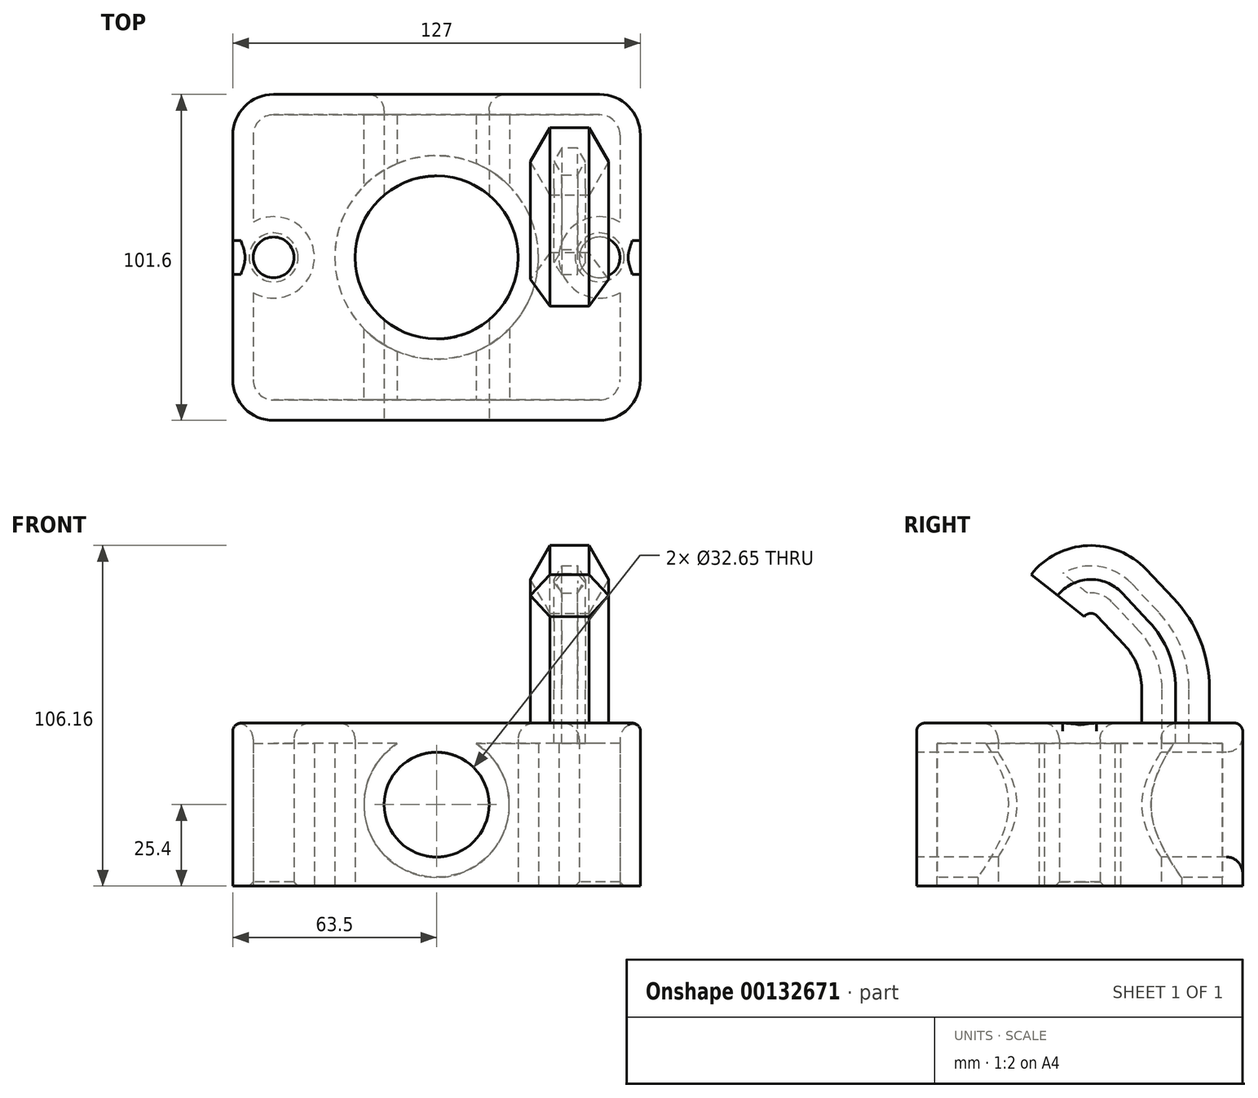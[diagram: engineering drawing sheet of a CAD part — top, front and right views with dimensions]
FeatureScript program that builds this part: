
annotation { "Feature Type Name" : "Feature", "Feature Type Description" : "" }
export const myFeature = defineFeature(function(context is Context, id is Id, definition is map)
    precondition{}
    {
        {
            var Q0;
            Q0=qCreatedBy(makeId("Top.planeOp"),FACE);
            var sketch = newSketch(context, id + "F0", { "sketchPlane" : qUnion([Q0])});
            skLineSegment(sketch, "E0.bottom", {"start": v(-63.5, 50.8) * mm, "end": v(63.5, 50.8) * mm});
            skLineSegment(sketch, "E0.top", {"start": v(-63.5, -50.8) * mm, "end": v(63.5, -50.8) * mm});
            skLineSegment(sketch, "E0.left", {"start": v(-63.5, 50.8) * mm, "end": v(-63.5, -50.8) * mm});
            skLineSegment(sketch, "E0.right", {"start": v(63.5, 50.8) * mm, "end": v(63.5, -50.8) * mm});
            skLineSegment(sketch, "E1", {"start": v(63.5, 50.8) * mm, "end": v(-63.5, -50.8) * mm, "construction": true});
            skCircle(sketch, "E2", {"center": v(0, 0) * mm, "radius": 25.4 * mm});
            skCircle(sketch, "E3", {"center": v(-50.8, 0) * mm, "radius": 6.35 * mm});
            skLineSegment(sketch, "E4", {"start": v(0, 0) * mm, "end": v(0, 50.8) * mm, "construction": true});
            skCircle(sketch, "E5.MirrorC", {"center": v(50.8, 0) * mm, "radius": 6.35 * mm});
            skSolve(sketch);
        }
        {
            var Q0;
            Q0 = qSketchRegion(id + "F0", true);
            extrude(context, id + "F1", {"entities" : qUnion([Q0]), "depth" : 50.8 * mm});
        }
        {
            var Q0;
            Q0=makeQuery(id+"F1.opExtrude","SWEPT_FACE",FACE,{"disambiguationData":[OSD([sQuery(id+"F0.wireOp",EDGE,"E0.top")])]});
            var sketch = newSketch(context, id + "F2", { "sketchPlane" : qUnion([Q0])});
            skCircle(sketch, "E6", {"center": v(0, 25.4) * mm, "radius": 16.33 * mm});
            skLineSegment(sketch, "E7", {"start": v(0, 0) * mm, "end": v(0, 50.8) * mm, "construction": true});
            skSolve(sketch);
        }
        {
            var Q0;
            Q0 = qSketchRegion(id + "F2", true);
            extrude(context, id + "F3", {"entities" : qUnion([Q0]), "operationType" : NewBodyOperationType.REMOVE, "endBound" : BoundingType.THROUGH_ALL, "oppositeDirection" : true, "depth" : 25.4 * mm});
        }
        {
            var Q0;
            Q0=makeQuery(id+"F1.opExtrude","CAP_EDGE",EDGE,{"disambiguationData":[OSD([sQuery(id+"F0.wireOp",EDGE,"E2")])],"isStart":false});
            var Q1;
            Q1=makeQuery(id+"F1.opExtrude","CAP_EDGE",EDGE,{"disambiguationData":[OSD([sQuery(id+"F0.wireOp",EDGE,"E3")])],"isStart":false});
            var Q2;
            Q2=makeQuery(id+"F1.opExtrude","CAP_EDGE",EDGE,{"disambiguationData":[OSD([sQuery(id+"F0.wireOp",EDGE,"E5.MirrorC")])],"isStart":false});
            var Q3;
            Q3=makeQuery(id+"F3.boolean.opBoolean","COPY",EDGE,{"derivedFrom":makeQuery(id+"F3.opExtrude","CAP_EDGE",EDGE,{"disambiguationData":[OSD([sQuery(id+"F2.wireOp",EDGE,"E6")])],"isStart":true})});
            var Q4;
            Q4=makeQuery(id+"F3.boolean.opBoolean","INTERSECT",EDGE,{"derivedFrom":[makeQuery(id+"F1.opExtrude","SWEPT_FACE",FACE,{"disambiguationData":[OSD([sQuery(id+"F0.wireOp",EDGE,"E0.bottom")])]}),makeQuery(id+"F3.opExtrude","SWEPT_FACE",FACE,{"disambiguationData":[OSD([sQuery(id+"F2.wireOp",EDGE,"E6")])]})]});
            fillet(context, id + "F4", {"entities" : qUnion([Q0, Q1, Q2, Q3, Q4]), "radius" : 5.08 * mm, "tangentPropagation" : true, "allowEdgeOverflow" : false});
        }
        {
            var Q0;
            Q0=makeQuery(id+"F1.opExtrude","SWEPT_EDGE",EDGE,{"disambiguationData":[OSD([sQuery(id+"F0.wireOp",EDGE,"E0.top"),sQuery(id+"F0.wireOp",EDGE,"E0.left")])]});
            var Q1;
            Q1=makeQuery(id+"F1.opExtrude","SWEPT_EDGE",EDGE,{"disambiguationData":[OSD([sQuery(id+"F0.wireOp",EDGE,"E0.top"),sQuery(id+"F0.wireOp",EDGE,"E0.right")])]});
            var Q2;
            Q2=makeQuery(id+"F1.opExtrude","SWEPT_EDGE",EDGE,{"disambiguationData":[OSD([sQuery(id+"F0.wireOp",EDGE,"E0.bottom"),sQuery(id+"F0.wireOp",EDGE,"E0.right")])]});
            var Q3;
            Q3=makeQuery(id+"F1.opExtrude","SWEPT_EDGE",EDGE,{"disambiguationData":[OSD([sQuery(id+"F0.wireOp",EDGE,"E0.bottom"),sQuery(id+"F0.wireOp",EDGE,"E0.left")])]});
            fillet(context, id + "F5", {"entities" : qUnion([Q0, Q1, Q2, Q3]), "radius" : 12.7 * mm, "tangentPropagation" : true, "allowEdgeOverflow" : false});
        }
        {
            var Q0;
            Q0=makeQuery(id+"F1.opExtrude","CAP_EDGE",EDGE,{"disambiguationData":[OSD([sQuery(id+"F0.wireOp",EDGE,"E0.right")])],"isStart":false});
            fillet(context, id + "F6", {"entities" : qUnion([Q0]), "radius" : 2.54 * mm, "tangentPropagation" : true, "allowEdgeOverflow" : false});
        }
        {
            var Q0;
            Q0=makeQuery(id+"F1.opExtrude","CAP_FACE",FACE,{"disambiguationData":[OSD([sQuery(id+"F0.wireOp",EDGE,"E0.bottom"),sQuery(id+"F0.wireOp",EDGE,"E0.top"),sQuery(id+"F0.wireOp",EDGE,"E0.left"),sQuery(id+"F0.wireOp",EDGE,"E0.right"),sQuery(id+"F0.wireOp",EDGE,"E2"),sQuery(id+"F0.wireOp",EDGE,"E3"),sQuery(id+"F0.wireOp",EDGE,"E5.MirrorC")])],"isStart":false});
            var sketch = newSketch(context, id + "F7", { "sketchPlane" : qUnion([Q0])});
            skCircle(sketch, "E8.cCircle", {"center": v(41.45, 29.89) * mm, "radius": 10.56 * mm, "construction": true});
            skLineSegment(sketch, "E8.0", {"start": v(29.26, 29.89) * mm, "end": v(35.36, 40.45) * mm});
            skLineSegment(sketch, "E8.1", {"start": v(35.36, 40.45) * mm, "end": v(47.55, 40.45) * mm});
            skLineSegment(sketch, "E8.2", {"start": v(47.55, 40.45) * mm, "end": v(53.65, 29.89) * mm});
            skLineSegment(sketch, "E8.3", {"start": v(53.65, 29.89) * mm, "end": v(47.55, 19.33) * mm});
            skLineSegment(sketch, "E8.4", {"start": v(47.55, 19.33) * mm, "end": v(35.36, 19.33) * mm});
            skLineSegment(sketch, "E8.5", {"start": v(35.36, 19.33) * mm, "end": v(29.26, 29.89) * mm});
            skPoint(sketch, "E8.0.midPoint", {"position": v(32.3, 35.17) * mm});
            skSolve(sketch);
        }
        {
            var Q0;
            Q0=qCreatedBy(makeId("Right.planeOp"),FACE);
            var Q1;
            Q1=sQuery(id+"F7.wireOp",VERTEX,"E8.cCircle.center");
            cPlane(context, id + "F8", {"entities" : qUnion([Q0, Q1]), "cplaneType" : CPlaneType.PLANE_POINT, "offset" : 25.4 * mm, "width" : 152.4 * mm, "height" : 152.4 * mm});
        }
        {
            var Q0;
            Q0=qCreatedBy(id+"F8.planeOp",FACE);
            var sketch = newSketch(context, id + "F9", { "sketchPlane" : qUnion([Q0])});
            skLineSegment(sketch, "E9", {"start": v(29.89, 50.8) * mm, "end": v(29.89, 61.52) * mm});
            skArc(sketch, "E10", {"start": v(29.89, 61.52) * mm, "mid": v(27.73, 72.8) * mm, "end": v(21.56, 82.48) * mm});
            skLineSegment(sketch, "E11", {"start": v(21.56, 82.48) * mm, "end": v(13.07, 91.47) * mm});
            skArc(sketch, "E12", {"start": v(13.07, 91.47) * mm, "mid": v(2.9, 95.58) * mm, "end": v(-6.85, 90.58) * mm});
            skSolve(sketch);
        }
        {
            var Q0;
            Q0 = qSketchRegion(id + "F7", true);
            var Q1;
            Q1 = qConstructionFilter(qBodyType(qCreatedBy(id + "F9" ,EDGE), BodyType.WIRE), ConstructionObject.NO);
            sweep(context, id + "F10", {"operationType" : NewBodyOperationType.ADD, "profiles" : qUnion([Q0]), "path" : qUnion([Q1])});
        }
        {
            var Q0;
            Q0=makeQuery(id+"F1.opExtrude","CAP_FACE",FACE,{"disambiguationData":[OSD([sQuery(id+"F0.wireOp",EDGE,"E0.bottom"),sQuery(id+"F0.wireOp",EDGE,"E0.top"),sQuery(id+"F0.wireOp",EDGE,"E0.left"),sQuery(id+"F0.wireOp",EDGE,"E0.right"),sQuery(id+"F0.wireOp",EDGE,"E2"),sQuery(id+"F0.wireOp",EDGE,"E3"),sQuery(id+"F0.wireOp",EDGE,"E5.MirrorC")])],"isStart":true});
            shell(context, id + "F11", {"entities" : qUnion([Q0]), "thickness" : 6.35 * mm});
        }
        {
            var Q0;
            Q0=makeQuery(id+"F1.opExtrude","CAP_EDGE",EDGE,{"disambiguationData":[OSD([sQuery(id+"F0.wireOp",EDGE,"E5.MirrorC")])],"isStart":true});
            var Q1;
            Q1=makeQuery(id+"F1.opExtrude","CAP_EDGE",EDGE,{"disambiguationData":[OSD([sQuery(id+"F0.wireOp",EDGE,"E3")])],"isStart":true});
            chamfer(context, id + "F12", {"entities" : qUnion([Q0, Q1]), "width" : 1.27 * mm, "tangentPropagation" : true});
        }
    });
